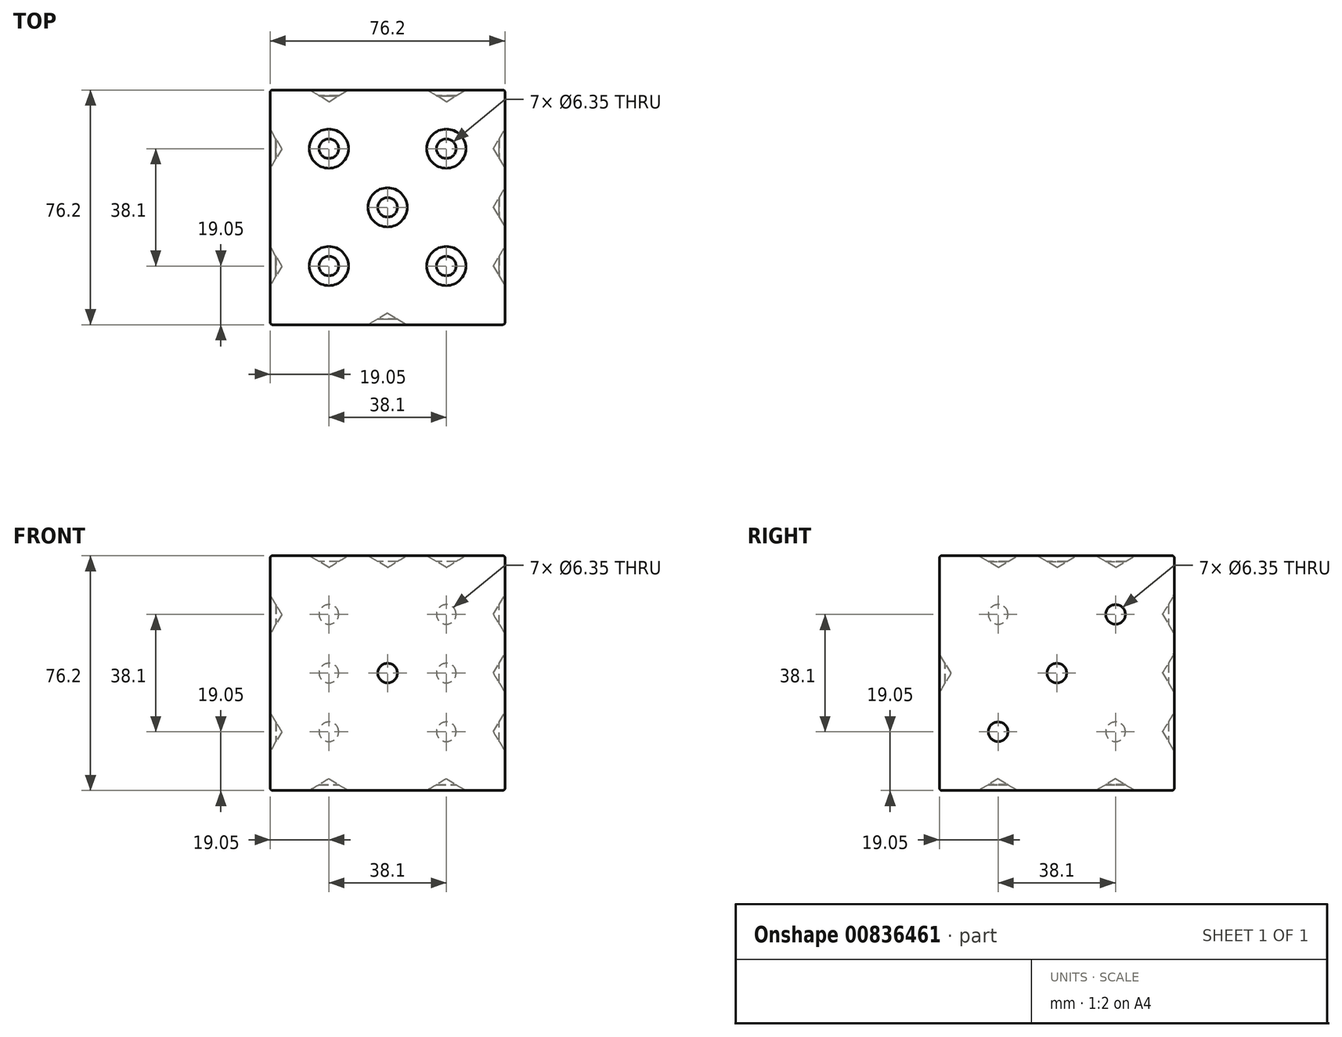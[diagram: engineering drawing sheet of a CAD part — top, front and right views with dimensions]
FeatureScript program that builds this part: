
annotation { "Feature Type Name" : "Feature", "Feature Type Description" : "" }
export const myFeature = defineFeature(function(context is Context, id is Id, definition is map)
    precondition{}
    {
        {
            var Q0;
            Q0=qCreatedBy(makeId("Front.planeOp"),FACE);
            var sketch = newSketch(context, id + "F0", { "sketchPlane" : qUnion([Q0])});
            skLineSegment(sketch, "E0.bottom", {"start": v(38.1, 38.1) * mm, "end": v(-38.1, 38.1) * mm});
            skLineSegment(sketch, "E0.top", {"start": v(38.1, -38.1) * mm, "end": v(-38.1, -38.1) * mm});
            skLineSegment(sketch, "E0.left", {"start": v(38.1, 38.1) * mm, "end": v(38.1, -38.1) * mm});
            skLineSegment(sketch, "E0.right", {"start": v(-38.1, 38.1) * mm, "end": v(-38.1, -38.1) * mm});
            skPoint(sketch, "E0.middle", {"position": v(0, 0) * mm});
            skLineSegment(sketch, "E1", {"start": v(-38.1, 0) * mm, "end": v(38.1, 0) * mm, "construction": true});
            skLineSegment(sketch, "E2", {"start": v(0, 38.1) * mm, "end": v(0, -38.1) * mm, "construction": true});
            skSolve(sketch);
        }
        {
            var Q0;
            Q0=makeQuery(id+"F0.imprint","IMPRINT",FACE,{"disambiguationData":[TD([[makeQuery(id+"F0.imprint","IMPRINT",EDGE,{"derivedFrom":sQuery(id+"F0.wireOp",EDGE,"E0.bottom")}),1.0]])]});
            extrude(context, id + "F1", {"entities" : qUnion([Q0]), "depth" : 76.2 * mm, "offsetDistance" : 25.4 * mm});
        }
        {
            var Q0;
            Q0=makeQuery(id+"F1.opExtrude","CAP_FACE",FACE,{"disambiguationData":[OSD([sQuery(id+"F0.wireOp",EDGE,"E0.bottom"),sQuery(id+"F0.wireOp",EDGE,"E0.top"),sQuery(id+"F0.wireOp",EDGE,"E0.left"),sQuery(id+"F0.wireOp",EDGE,"E0.right")])],"isStart":true});
            var sketch = newSketch(context, id + "F2", { "sketchPlane" : qUnion([Q0])});
            skLineSegment(sketch, "E3", {"start": v(0, 38.1) * mm, "end": v(0, -38.1) * mm, "construction": true});
            skLineSegment(sketch, "E4", {"start": v(-38.1, 0) * mm, "end": v(38.1, 0) * mm, "construction": true});
            skLineSegment(sketch, "E5", {"start": v(38.1, 38.1) * mm, "end": v(19.05, 38.1) * mm, "construction": true});
            skLineSegment(sketch, "E6", {"start": v(38.1, 38.1) * mm, "end": v(38.1, -19.05) * mm});
            skLineSegment(sketch, "E7", {"start": v(38.1, 38.1) * mm, "end": v(-19.05, 38.1) * mm, "construction": true});
            skLineSegment(sketch, "E8", {"start": v(38.1, 38.1) * mm, "end": v(38.1, 19.05) * mm, "construction": true});
            skLineSegment(sketch, "E9", {"start": v(19.05, 38.1) * mm, "end": v(19.05, -38.1) * mm, "construction": true});
            skLineSegment(sketch, "E10", {"start": v(-19.05, 38.1) * mm, "end": v(-19.05, -38.1) * mm, "construction": true});
            skLineSegment(sketch, "E11", {"start": v(38.1, -19.05) * mm, "end": v(-38.1, -19.05) * mm, "construction": true});
            skLineSegment(sketch, "E12", {"start": v(38.1, 19.05) * mm, "end": v(-38.1, 19.05) * mm, "construction": true});
            skPoint(sketch, "E13", {"position": v(0, 0) * mm});
            skPoint(sketch, "E14", {"position": v(-19.05, 19.05) * mm});
            skPoint(sketch, "E15", {"position": v(19.05, 19.05) * mm});
            skPoint(sketch, "E16", {"position": v(19.05, -19.05) * mm});
            skPoint(sketch, "E17", {"position": v(-19.05, -19.05) * mm});
            skPoint(sketch, "E18", {"position": v(-19.05, 0) * mm});
            skPoint(sketch, "E19", {"position": v(19.05, 0) * mm});
            skSolve(sketch);
        }
        {
            var Q0;
            Q0=makeQuery(id+"F1.opExtrude","CAP_FACE",FACE,{"disambiguationData":[OSD([sQuery(id+"F0.wireOp",EDGE,"E0.bottom"),sQuery(id+"F0.wireOp",EDGE,"E0.top"),sQuery(id+"F0.wireOp",EDGE,"E0.left"),sQuery(id+"F0.wireOp",EDGE,"E0.right")])],"isStart":false});
            var sketch = newSketch(context, id + "F3", { "sketchPlane" : qUnion([Q0])});
            skPoint(sketch, "E20", {"position": v(0, 0) * mm});
            skSolve(sketch);
        }
        {
            var Q0;
            Q0=sQuery(id+"F2.wireOp",VERTEX,"E16");
            var Q1;
            Q1=sQuery(id+"F2.wireOp",VERTEX,"E17");
            var Q2;
            Q2=sQuery(id+"F2.wireOp",VERTEX,"E18");
            var Q3;
            Q3=sQuery(id+"F2.wireOp",VERTEX,"E14");
            var Q4;
            Q4=sQuery(id+"F2.wireOp",VERTEX,"E15");
            var Q5;
            Q5=sQuery(id+"F2.wireOp",VERTEX,"E19");
            var Q6;
            Q6=makeQuery(id+"F1.opExtrude","SWEPT_BODY",BODY,{"disambiguationData":[OSD([sQuery(id+"F0.wireOp",EDGE,"E0.bottom"),sQuery(id+"F0.wireOp",EDGE,"E0.top"),sQuery(id+"F0.wireOp",EDGE,"E0.left"),sQuery(id+"F0.wireOp",EDGE,"E0.right")])]});
            hole(context, id + "F4", {"style" : HoleStyle.C_SINK, "endStyle" : HoleEndStyle.BLIND, "holeDiameter" : 6.35 * mm, "cSinkDiameter" : 12.7 * mm, "cSinkAngle" : 120 * degree, "majorDiameter" : 6.35 * mm, "holeDepth" : 1.9 * mm, "isTappedThrough" : true, "tappedDepth" : 12.7 * mm, "tapClearance" : 3, "locations" : qUnion([Q0, Q1, Q2, Q3, Q4, Q5]), "scope" : qUnion([Q6])});
        }
        {
            var Q0;
            Q0=sQuery(id+"F3.wireOp",VERTEX,"E20");
            var Q1;
            Q1=makeQuery(id+"F1.opExtrude","SWEPT_BODY",BODY,{"disambiguationData":[OSD([sQuery(id+"F0.wireOp",EDGE,"E0.bottom"),sQuery(id+"F0.wireOp",EDGE,"E0.top"),sQuery(id+"F0.wireOp",EDGE,"E0.left"),sQuery(id+"F0.wireOp",EDGE,"E0.right")])]});
            hole(context, id + "F5", {"style" : HoleStyle.C_SINK, "endStyle" : HoleEndStyle.BLIND, "holeDiameter" : 6.35 * mm, "cSinkDiameter" : 12.7 * mm, "cSinkAngle" : 120 * degree, "majorDiameter" : 6.35 * mm, "holeDepth" : 1.9 * mm, "isTappedThrough" : true, "tappedDepth" : 12.7 * mm, "tapClearance" : 3, "locations" : qUnion([Q0]), "scope" : qUnion([Q1])});
        }
        {
            var Q0;
            Q0=makeQuery(id+"F1.opExtrude","SWEPT_FACE",FACE,{"disambiguationData":[OSD([sQuery(id+"F0.wireOp",EDGE,"E0.right")])]});
            var sketch = newSketch(context, id + "F6", { "sketchPlane" : qUnion([Q0])});
            skLineSegment(sketch, "E21", {"start": v(0, 0) * mm, "end": v(76.2, 0) * mm, "construction": true});
            skLineSegment(sketch, "E22", {"start": v(38.1, -38.1) * mm, "end": v(38.1, 38.1) * mm, "construction": true});
            skLineSegment(sketch, "E23", {"start": v(0, 38.1) * mm, "end": v(0, -19.05) * mm, "construction": true});
            skLineSegment(sketch, "E24", {"start": v(0, 38.1) * mm, "end": v(0, 19.05) * mm, "construction": true});
            skLineSegment(sketch, "E25", {"start": v(0, 38.1) * mm, "end": v(57.15, 38.1) * mm, "construction": true});
            skLineSegment(sketch, "E26", {"start": v(0, 38.1) * mm, "end": v(19.05, 38.1) * mm, "construction": true});
            skLineSegment(sketch, "E27", {"start": v(0, 19.05) * mm, "end": v(76.2, 19.05) * mm, "construction": true});
            skLineSegment(sketch, "E28", {"start": v(0, -19.05) * mm, "end": v(76.2, -19.05) * mm, "construction": true});
            skLineSegment(sketch, "E29", {"start": v(19.05, 38.1) * mm, "end": v(19.05, -38.1) * mm, "construction": true});
            skLineSegment(sketch, "E30", {"start": v(57.15, 38.1) * mm, "end": v(57.15, -38.1) * mm, "construction": true});
            skPoint(sketch, "E31", {"position": v(19.05, -19.05) * mm});
            skPoint(sketch, "E32", {"position": v(19.05, 19.05) * mm});
            skPoint(sketch, "E33", {"position": v(57.15, 19.05) * mm});
            skPoint(sketch, "E34", {"position": v(57.15, -19.05) * mm});
            skSolve(sketch);
        }
        {
            var Q0;
            Q0=sQuery(id+"F6.wireOp",VERTEX,"E31");
            var Q1;
            Q1=sQuery(id+"F6.wireOp",VERTEX,"E32");
            var Q2;
            Q2=sQuery(id+"F6.wireOp",VERTEX,"E33");
            var Q3;
            Q3=sQuery(id+"F6.wireOp",VERTEX,"E34");
            var Q4;
            Q4=makeQuery(id+"F1.opExtrude","SWEPT_BODY",BODY,{"disambiguationData":[OSD([sQuery(id+"F0.wireOp",EDGE,"E0.bottom"),sQuery(id+"F0.wireOp",EDGE,"E0.top"),sQuery(id+"F0.wireOp",EDGE,"E0.left"),sQuery(id+"F0.wireOp",EDGE,"E0.right")])]});
            hole(context, id + "F7", {"style" : HoleStyle.C_SINK, "endStyle" : HoleEndStyle.BLIND, "holeDiameter" : 6.35 * mm, "cSinkDiameter" : 12.7 * mm, "cSinkAngle" : 120 * degree, "majorDiameter" : 6.35 * mm, "holeDepth" : 1.9 * mm, "isTappedThrough" : true, "tappedDepth" : 12.7 * mm, "tapClearance" : 3, "locations" : qUnion([Q0, Q1, Q2, Q3]), "scope" : qUnion([Q4])});
        }
        {
            var Q0;
            Q0=makeQuery(id+"F1.opExtrude","SWEPT_FACE",FACE,{"disambiguationData":[OSD([sQuery(id+"F0.wireOp",EDGE,"E0.left")])]});
            var sketch = newSketch(context, id + "F8", { "sketchPlane" : qUnion([Q0])});
            skLineSegment(sketch, "E35", {"start": v(-76.2, -38.1) * mm, "end": v(-57.15, -38.1) * mm, "construction": true});
            skLineSegment(sketch, "E36", {"start": v(-76.2, -38.1) * mm, "end": v(-19.05, -38.1) * mm, "construction": true});
            skLineSegment(sketch, "E37", {"start": v(-76.2, -38.1) * mm, "end": v(-76.2, -19.05) * mm, "construction": true});
            skLineSegment(sketch, "E38", {"start": v(-76.2, -38.1) * mm, "end": v(-76.2, 19.05) * mm, "construction": true});
            skPoint(sketch, "E39", {"position": v(-76.2, 0) * mm});
            skLineSegment(sketch, "E40", {"start": v(-76.2, 0) * mm, "end": v(-38.1, 0) * mm, "construction": true});
            skPoint(sketch, "E41", {"position": v(-38.1, 0) * mm});
            skLineSegment(sketch, "E42", {"start": v(-57.15, -38.1) * mm, "end": v(-57.15, 38.1) * mm, "construction": true});
            skLineSegment(sketch, "E43", {"start": v(-76.2, 19.05) * mm, "end": v(0, 19.05) * mm, "construction": true});
            skLineSegment(sketch, "E44", {"start": v(-19.05, -38.1) * mm, "end": v(-19.05, 38.1) * mm, "construction": true});
            skLineSegment(sketch, "E45", {"start": v(-76.2, -19.05) * mm, "end": v(0, -19.05) * mm, "construction": true});
            skPoint(sketch, "E46", {"position": v(-57.15, -19.05) * mm});
            skPoint(sketch, "E47", {"position": v(-19.05, 19.05) * mm});
            skSolve(sketch);
        }
        {
            var Q0;
            Q0=sQuery(id+"F8.wireOp",VERTEX,"E46");
            var Q1;
            Q1=sQuery(id+"F8.wireOp",VERTEX,"E41");
            var Q2;
            Q2=sQuery(id+"F8.wireOp",VERTEX,"E47");
            var Q3;
            Q3=makeQuery(id+"F1.opExtrude","SWEPT_BODY",BODY,{"disambiguationData":[OSD([sQuery(id+"F0.wireOp",EDGE,"E0.bottom"),sQuery(id+"F0.wireOp",EDGE,"E0.top"),sQuery(id+"F0.wireOp",EDGE,"E0.left"),sQuery(id+"F0.wireOp",EDGE,"E0.right")])]});
            hole(context, id + "F9", {"style" : HoleStyle.C_SINK, "endStyle" : HoleEndStyle.BLIND, "holeDiameter" : 6.35 * mm, "cSinkDiameter" : 12.7 * mm, "cSinkAngle" : 120 * degree, "majorDiameter" : 6.35 * mm, "holeDepth" : 1.9 * mm, "isTappedThrough" : true, "tappedDepth" : 12.7 * mm, "tapClearance" : 3, "locations" : qUnion([Q0, Q1, Q2]), "scope" : qUnion([Q3])});
        }
        {
            var Q0;
            Q0=makeQuery(id+"F1.opExtrude","SWEPT_FACE",FACE,{"disambiguationData":[OSD([sQuery(id+"F0.wireOp",EDGE,"E0.top")])]});
            var sketch = newSketch(context, id + "F10", { "sketchPlane" : qUnion([Q0])});
            skPoint(sketch, "E48", {"position": v(38.1, 0) * mm});
            skPoint(sketch, "E49", {"position": v(-38.1, 0) * mm});
            skPoint(sketch, "E50", {"position": v(-38.1, 38.1) * mm});
            skPoint(sketch, "E51", {"position": v(-38.1, 76.2) * mm});
            skPoint(sketch, "E52", {"position": v(0, 76.2) * mm});
            skPoint(sketch, "E53", {"position": v(38.1, 76.2) * mm});
            skPoint(sketch, "E54", {"position": v(38.1, 38.1) * mm});
            skPoint(sketch, "E55", {"position": v(0, 38.1) * mm});
            skPoint(sketch, "E55.positionSnap0", {"position": v(0, 0) * mm});
            skLineSegment(sketch, "E56", {"start": v(-38.1, 0) * mm, "end": v(-19.05, 0) * mm, "construction": true});
            skLineSegment(sketch, "E57", {"start": v(-38.1, 0) * mm, "end": v(19.05, 0) * mm, "construction": true});
            skLineSegment(sketch, "E58", {"start": v(-38.1, 0) * mm, "end": v(-38.1, 19.05) * mm, "construction": true});
            skLineSegment(sketch, "E59", {"start": v(-38.1, 0) * mm, "end": v(-38.1, 57.15) * mm, "construction": true});
            skLineSegment(sketch, "E60", {"start": v(19.05, 0) * mm, "end": v(19.05, 76.2) * mm, "construction": true});
            skLineSegment(sketch, "E61", {"start": v(-19.05, 0) * mm, "end": v(-19.05, 76.2) * mm, "construction": true});
            skLineSegment(sketch, "E62", {"start": v(-38.1, 19.05) * mm, "end": v(38.1, 19.05) * mm, "construction": true});
            skLineSegment(sketch, "E63", {"start": v(-38.1, 57.15) * mm, "end": v(38.1, 57.15) * mm, "construction": true});
            skPoint(sketch, "E64", {"position": v(-19.05, 19.05) * mm});
            skPoint(sketch, "E65", {"position": v(19.05, 57.15) * mm});
            skSolve(sketch);
        }
        {
            var Q0;
            Q0=sQuery(id+"F10.wireOp",VERTEX,"E64");
            var Q1;
            Q1=sQuery(id+"F10.wireOp",VERTEX,"E65");
            var Q2;
            Q2=makeQuery(id+"F1.opExtrude","SWEPT_BODY",BODY,{"disambiguationData":[OSD([sQuery(id+"F0.wireOp",EDGE,"E0.bottom"),sQuery(id+"F0.wireOp",EDGE,"E0.top"),sQuery(id+"F0.wireOp",EDGE,"E0.left"),sQuery(id+"F0.wireOp",EDGE,"E0.right")])]});
            hole(context, id + "F11", {"style" : HoleStyle.C_SINK, "endStyle" : HoleEndStyle.BLIND, "holeDiameter" : 6.35 * mm, "cSinkDiameter" : 12.7 * mm, "cSinkAngle" : 120 * degree, "majorDiameter" : 6.35 * mm, "holeDepth" : 1.9 * mm, "isTappedThrough" : true, "tappedDepth" : 12.7 * mm, "tapClearance" : 3, "locations" : qUnion([Q0, Q1]), "scope" : qUnion([Q2])});
        }
        {
            var Q0;
            Q0=makeQuery(id+"F1.opExtrude","SWEPT_FACE",FACE,{"disambiguationData":[OSD([sQuery(id+"F0.wireOp",EDGE,"E0.bottom")])]});
            var sketch = newSketch(context, id + "F12", { "sketchPlane" : qUnion([Q0])});
            skPoint(sketch, "E66", {"position": v(-38.1, 0) * mm});
            skPoint(sketch, "E67", {"position": v(0, 0) * mm});
            skPoint(sketch, "E68", {"position": v(38.1, 0) * mm});
            skPoint(sketch, "E69", {"position": v(38.1, -38.1) * mm});
            skPoint(sketch, "E70", {"position": v(38.1, -76.2) * mm});
            skPoint(sketch, "E71", {"position": v(0, -76.2) * mm});
            skPoint(sketch, "E72", {"position": v(-38.1, -76.2) * mm});
            skPoint(sketch, "E73", {"position": v(-38.1, -38.1) * mm});
            skPoint(sketch, "E74", {"position": v(0, -38.1) * mm});
            skLineSegment(sketch, "E75", {"start": v(38.1, 0) * mm, "end": v(19.05, 0) * mm, "construction": true});
            skLineSegment(sketch, "E76", {"start": v(38.1, 0) * mm, "end": v(-19.05, 0) * mm, "construction": true});
            skLineSegment(sketch, "E77", {"start": v(38.1, 0) * mm, "end": v(38.1, -19.05) * mm, "construction": true});
            skLineSegment(sketch, "E78", {"start": v(38.1, 0) * mm, "end": v(38.1, -57.15) * mm, "construction": true});
            skLineSegment(sketch, "E79", {"start": v(19.05, 0) * mm, "end": v(19.05, -76.2) * mm, "construction": true});
            skLineSegment(sketch, "E80", {"start": v(-19.05, 0) * mm, "end": v(-19.05, -76.2) * mm, "construction": true});
            skLineSegment(sketch, "E81", {"start": v(38.1, -19.05) * mm, "end": v(-38.1, -19.05) * mm, "construction": true});
            skLineSegment(sketch, "E82", {"start": v(38.1, -57.15) * mm, "end": v(-38.1, -57.15) * mm, "construction": true});
            skPoint(sketch, "E83", {"position": v(-19.05, -19.05) * mm});
            skPoint(sketch, "E84", {"position": v(19.05, -19.05) * mm});
            skPoint(sketch, "E85", {"position": v(19.05, -57.15) * mm});
            skPoint(sketch, "E86", {"position": v(-19.05, -57.15) * mm});
            skSolve(sketch);
        }
        {
            var Q0;
            Q0=sQuery(id+"F12.wireOp",VERTEX,"E83");
            var Q1;
            Q1=sQuery(id+"F12.wireOp",VERTEX,"E84");
            var Q2;
            Q2=sQuery(id+"F12.wireOp",VERTEX,"E74");
            var Q3;
            Q3=sQuery(id+"F12.wireOp",VERTEX,"E85");
            var Q4;
            Q4=sQuery(id+"F12.wireOp",VERTEX,"E86");
            var Q5;
            Q5=makeQuery(id+"F1.opExtrude","SWEPT_BODY",BODY,{"disambiguationData":[OSD([sQuery(id+"F0.wireOp",EDGE,"E0.bottom"),sQuery(id+"F0.wireOp",EDGE,"E0.top"),sQuery(id+"F0.wireOp",EDGE,"E0.left"),sQuery(id+"F0.wireOp",EDGE,"E0.right")])]});
            hole(context, id + "F13", {"style" : HoleStyle.C_SINK, "endStyle" : HoleEndStyle.BLIND, "holeDiameter" : 6.35 * mm, "cSinkDiameter" : 12.7 * mm, "cSinkAngle" : 120 * degree, "majorDiameter" : 6.35 * mm, "holeDepth" : 1.9 * mm, "isTappedThrough" : true, "tappedDepth" : 12.7 * mm, "tapClearance" : 3, "locations" : qUnion([Q0, Q1, Q2, Q3, Q4]), "scope" : qUnion([Q5])});
        }
        {
            var Q0;
            Q0=makeQuery(id+"F1.opExtrude","CAP_FACE",FACE,{"disambiguationData":[OSD([sQuery(id+"F0.wireOp",EDGE,"E0.bottom"),sQuery(id+"F0.wireOp",EDGE,"E0.top"),sQuery(id+"F0.wireOp",EDGE,"E0.left"),sQuery(id+"F0.wireOp",EDGE,"E0.right")])],"isStart":false});
            fillet(context, id + "F14", {"entities" : qUnion([Q0]), "radius" : 0.76 * mm, "tangentPropagation" : true, "allowEdgeOverflow" : false});
        }
        {
            var Q0;
            Q0=makeQuery(id+"F1.opExtrude","SWEPT_FACE",FACE,{"disambiguationData":[OSD([sQuery(id+"F0.wireOp",EDGE,"E0.left")])]});
            fillet(context, id + "F15", {"entities" : qUnion([Q0]), "radius" : 0.76 * mm, "tangentPropagation" : true, "allowEdgeOverflow" : false});
        }
        {
            var Q0;
            Q0=makeQuery(id+"F1.opExtrude","CAP_FACE",FACE,{"disambiguationData":[OSD([sQuery(id+"F0.wireOp",EDGE,"E0.bottom"),sQuery(id+"F0.wireOp",EDGE,"E0.top"),sQuery(id+"F0.wireOp",EDGE,"E0.left"),sQuery(id+"F0.wireOp",EDGE,"E0.right")])],"isStart":true});
            fillet(context, id + "F16", {"entities" : qUnion([Q0]), "radius" : 0.76 * mm, "tangentPropagation" : true, "allowEdgeOverflow" : false});
        }
        {
            var Q0;
            Q0=makeQuery(id+"F1.opExtrude","SWEPT_FACE",FACE,{"disambiguationData":[OSD([sQuery(id+"F0.wireOp",EDGE,"E0.right")])]});
            fillet(context, id + "F17", {"entities" : qUnion([Q0]), "radius" : 0.76 * mm, "tangentPropagation" : true, "allowEdgeOverflow" : false});
        }
    });
